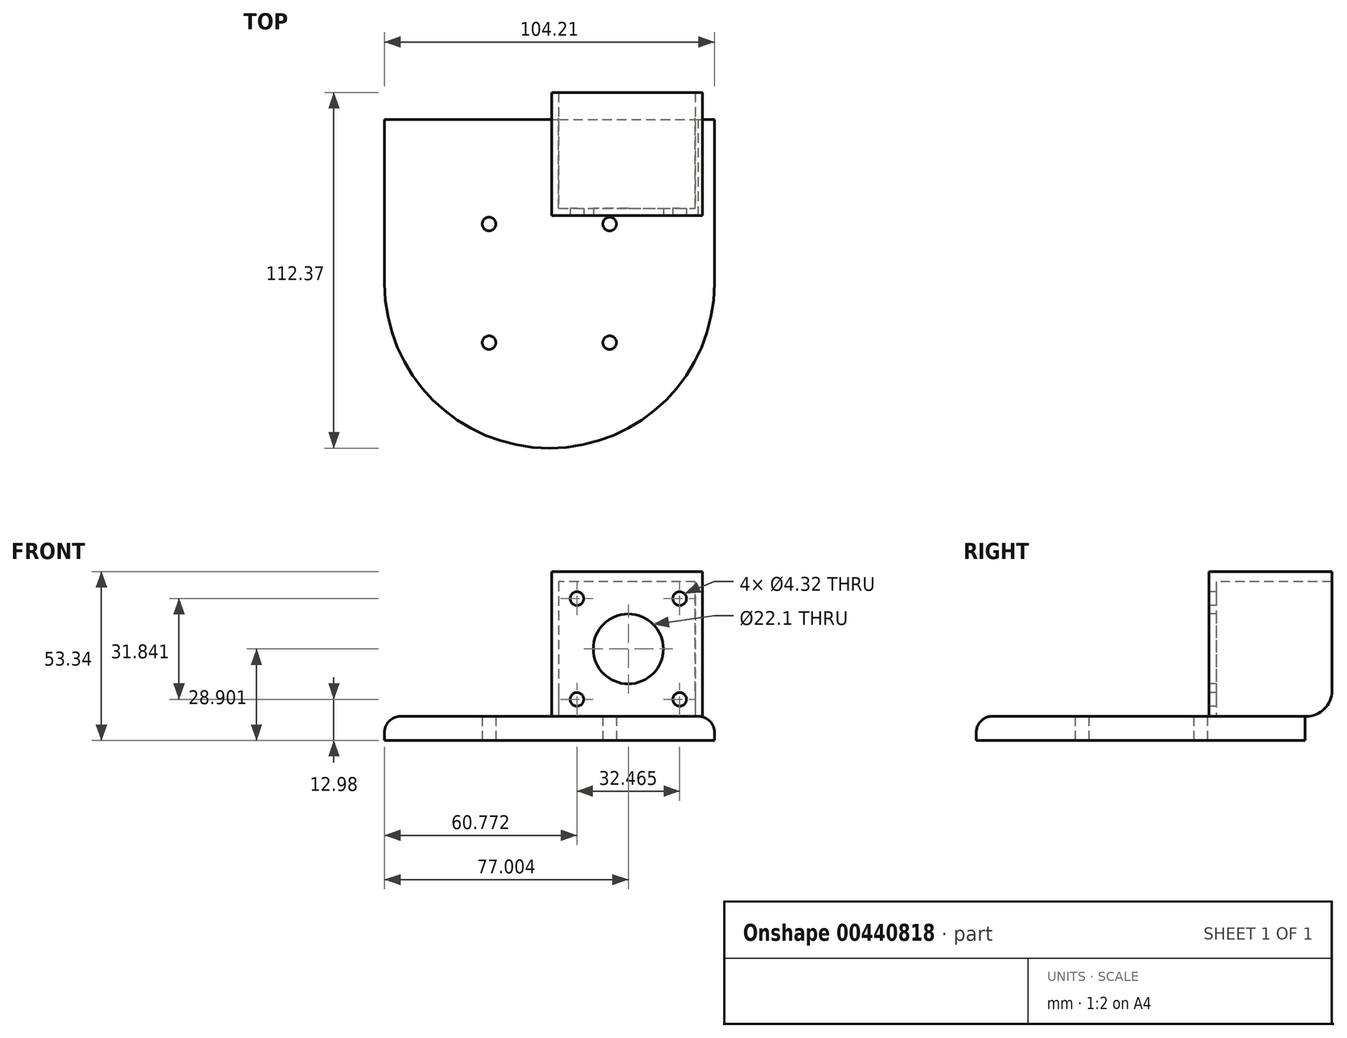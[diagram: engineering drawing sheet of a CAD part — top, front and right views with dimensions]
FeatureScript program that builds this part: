
annotation { "Feature Type Name" : "Feature", "Feature Type Description" : "" }
export const myFeature = defineFeature(function(context is Context, id is Id, definition is map)
    precondition{}
    {
        {
            var Q0;
            Q0=qCreatedBy(makeId("Top.planeOp"),FACE);
            var sketch = newSketch(context, id + "F0", { "sketchPlane" : qUnion([Q0])});
            skLineSegment(sketch, "E0.bottom", {"start": v(19.05, 18.75) * mm, "end": v(-19.05, 18.75) * mm});
            skLineSegment(sketch, "E0.top", {"start": v(19.05, -19.35) * mm, "end": v(-19.05, -19.35) * mm});
            skLineSegment(sketch, "E0.left", {"start": v(19.05, 18.75) * mm, "end": v(19.05, -19.35) * mm});
            skLineSegment(sketch, "E0.right", {"start": v(-19.05, 18.75) * mm, "end": v(-19.05, -19.35) * mm});
            skPoint(sketch, "E0.middle", {"position": v(0, -0.3) * mm});
            skCircle(sketch, "E1", {"center": v(-19.05, 18.75) * mm, "radius": 2.16 * mm});
            skCircle(sketch, "E2.MirrorC", {"center": v(19.05, 18.75) * mm, "radius": 2.16 * mm});
            skCircle(sketch, "E3.MirrorC", {"center": v(19.05, -18.75) * mm, "radius": 2.16 * mm});
            skCircle(sketch, "E4.MirrorC", {"center": v(-19.05, -18.75) * mm, "radius": 2.16 * mm});
            skLineSegment(sketch, "E5.bottom", {"start": v(-52.07, 0) * mm, "end": v(52.14, 0) * mm});
            skLineSegment(sketch, "E5.top", {"start": v(-52.07, 51.72) * mm, "end": v(52.14, 51.72) * mm});
            skLineSegment(sketch, "E5.left", {"start": v(-52.07, 0) * mm, "end": v(-52.07, 51.72) * mm});
            skLineSegment(sketch, "E5.right", {"start": v(52.14, 0) * mm, "end": v(52.14, 51.72) * mm});
            skArc(sketch, "E6", {"start": v(-52.07, 0) * mm, "mid": v(0.03, -52.1) * mm, "end": v(52.14, 0) * mm});
            skSolve(sketch);
        }
        {
            var Q0;
            Q0 = qSketchRegion(id + "F0", true);
            var Q1;
            {var subQ5=sQuery(id+"F0.wireOp",EDGE,"E2.MirrorC");var subQ13=sQuery(id+"F0.wireOp",EDGE,"E0.bottom");var subQ14=makeQuery(id+"F0.imprint","INTERSECT",VERTEX,{"derivedFrom":[subQ13,subQ5]});Q1=makeQuery(id+"F0.imprint","IMPRINT",FACE,{"disambiguationData":[TD([[makeQuery(id+"F0.imprint","IMPRINT",EDGE,{"disambiguationData":[TD([[subQ14,-1.0]])],"derivedFrom":subQ13}),1.0]])]});}
            var Q2;
            {var subQ7=sQuery(id+"F0.wireOp",EDGE,"E3.MirrorC");var subQ9=sQuery(id+"F0.wireOp",EDGE,"E0.top");var subQ10=makeQuery(id+"F0.imprint","INTERSECT",VERTEX,{"derivedFrom":[subQ9,subQ7]});Q2=makeQuery(id+"F0.imprint","IMPRINT",FACE,{"disambiguationData":[TD([[makeQuery(id+"F0.imprint","IMPRINT",EDGE,{"disambiguationData":[TD([[subQ10,-1.0]])],"derivedFrom":subQ9}),-1.0]])]});}
            extrude(context, id + "F1", {"entities" : qUnion([Q0, Q1, Q2]), "depth" : 7.62 * mm});
        }
        {
            var Q0;
            Q0=makeQuery(id+"F1.opExtrude","CAP_EDGE",EDGE,{"disambiguationData":[OSD([sQuery(id+"F0.wireOp",EDGE,"E6")])],"isStart":false});
            fillet(context, id + "F2", {"entities" : qUnion([Q0]), "radius" : 5.08 * mm, "tangentPropagation" : true, "allowEdgeOverflow" : false});
        }
        {
            var Q0;
            Q0=makeQuery(id+"F1.opExtrude","CAP_FACE",FACE,{"disambiguationData":[OSD([sQuery(id+"F0.wireOp",EDGE,"LegbURL5-L06y-lJQr-4DTz-lo4QkHgCWNkF"),sQuery(id+"F0.wireOp",EDGE,"E1"),sQuery(id+"F0.wireOp",EDGE,"E2.MirrorC"),sQuery(id+"F0.wireOp",EDGE,"E3.MirrorC"),sQuery(id+"F0.wireOp",EDGE,"E4.MirrorC")])],"isStart":false});
            var sketch = newSketch(context, id + "F3", { "sketchPlane" : qUnion([Q0])});
            skLineSegment(sketch, "E7.bottom", {"start": v(2.95, 23.69) * mm, "end": v(46.13, 23.69) * mm});
            skLineSegment(sketch, "E7.left", {"start": v(2.95, 23.69) * mm, "end": v(2.95, 57.98) * mm});
            skLineSegment(sketch, "E7.right", {"start": v(46.13, 23.69) * mm, "end": v(46.13, 57.98) * mm});
            skPoint(sketch, "E7.middle", {"position": v(24.54, 40.83) * mm});
            skLineSegment(sketch, "E8.bottom", {"start": v(48.4, 21.4) * mm, "end": v(0.69, 21.4) * mm});
            skLineSegment(sketch, "E8.left", {"start": v(48.4, 21.4) * mm, "end": v(48.4, 60.27) * mm});
            skLineSegment(sketch, "E8.right", {"start": v(0.69, 21.4) * mm, "end": v(0.69, 60.27) * mm});
            skLineSegment(sketch, "E9", {"start": v(2.95, 57.98) * mm, "end": v(2.95, 60.27) * mm});
            skLineSegment(sketch, "E10", {"start": v(2.95, 60.27) * mm, "end": v(0.69, 60.27) * mm});
            skLineSegment(sketch, "E11", {"start": v(46.13, 57.98) * mm, "end": v(46.13, 60.27) * mm});
            skLineSegment(sketch, "E12", {"start": v(46.13, 60.27) * mm, "end": v(48.4, 60.27) * mm});
            skSolve(sketch);
        }
        {
            var Q0;
            Q0 = qSketchRegion(id + "F3", true);
            extrude(context, id + "F4", {"entities" : qUnion([Q0]), "operationType" : NewBodyOperationType.ADD, "depth" : 45.72 * mm});
        }
        {
            var Q0;
            Q0=makeQuery(id+"F4.opExtrude","SWEPT_FACE",FACE,{"disambiguationData":[OSD([sQuery(id+"F3.wireOp",EDGE,"E8.bottom")])]});
            var sketch = newSketch(context, id + "F5", { "sketchPlane" : qUnion([Q0])});
            skPoint(sketch, "E13.centerSnap0", {"position": v(1.08, 30.47) * mm});
            skLineSegment(sketch, "E14", {"start": v(8.7, 44.82) * mm, "end": v(1.08, 44.82) * mm});
            skCircle(sketch, "E15", {"center": v(8.7, 44.82) * mm, "radius": 2.16 * mm});
            skLineSegment(sketch, "E16", {"start": v(24.93, 38.95) * mm, "end": v(24.93, 53.33) * mm});
            skCircle(sketch, "E17", {"center": v(24.93, 28.9) * mm, "radius": 11.05 * mm});
            skLineSegment(sketch, "E18", {"start": v(8.7, 46.98) * mm, "end": v(8.7, 53.33) * mm});
            skLineSegment(sketch, "E19.MirrorCS", {"start": v(41.17, 44.82) * mm, "end": v(48.79, 44.82) * mm});
            skLineSegment(sketch, "E20.MirrorCS", {"start": v(41.17, 46.98) * mm, "end": v(41.17, 53.33) * mm});
            skCircle(sketch, "E21.MirrorC", {"center": v(41.17, 44.82) * mm, "radius": 2.16 * mm});
            skLineSegment(sketch, "E22", {"start": v(24.93, 28.9) * mm, "end": v(29.7, 28.9) * mm});
            skCircle(sketch, "E23.MirrorC", {"center": v(41.17, 12.98) * mm, "radius": 2.16 * mm});
            skCircle(sketch, "E24.MirrorC", {"center": v(8.7, 12.98) * mm, "radius": 2.16 * mm});
            skLineSegment(sketch, "E25.MirrorCS", {"start": v(8.7, 10.82) * mm, "end": v(8.7, 4.47) * mm});
            skLineSegment(sketch, "E26.MirrorCS", {"start": v(8.7, 12.98) * mm, "end": v(1.08, 12.98) * mm});
            skLineSegment(sketch, "E27.MirrorCS", {"start": v(41.17, 10.82) * mm, "end": v(41.17, 4.47) * mm});
            skLineSegment(sketch, "E28.MirrorCS", {"start": v(41.17, 12.98) * mm, "end": v(48.79, 12.98) * mm});
            skSolve(sketch);
        }
        {
            var Q0;
            Q0 = qSketchRegion(id + "F5", true);
            extrude(context, id + "F6", {"entities" : qUnion([Q0]), "operationType" : NewBodyOperationType.REMOVE, "oppositeDirection" : true, "depth" : 25.4 * mm});
        }
        {
            var Q0;
            Q0=makeQuery(id+"F4.opExtrude","SWEPT_FACE",FACE,{"disambiguationData":[OSD([sQuery(id+"F3.wireOp",EDGE,"E7.bottom")])]});
            var sketch = newSketch(context, id + "F7", { "sketchPlane" : qUnion([Q0])});
            skLineSegment(sketch, "E29.bottom", {"start": v(-46.13, 53.34) * mm, "end": v(-2.95, 53.34) * mm});
            skLineSegment(sketch, "E29.top", {"start": v(-46.13, 50.17) * mm, "end": v(-2.95, 50.17) * mm});
            skLineSegment(sketch, "E29.left", {"start": v(-46.13, 53.34) * mm, "end": v(-46.13, 50.17) * mm});
            skLineSegment(sketch, "E29.right", {"start": v(-2.95, 53.34) * mm, "end": v(-2.95, 50.17) * mm});
            skSolve(sketch);
        }
        {
            var Q0;
            Q0=makeQuery(id+"F7.imprint","IMPRINT",FACE,{"disambiguationData":[TD([[makeQuery(id+"F7.imprint","IMPRINT",EDGE,{"derivedFrom":sQuery(id+"F7.wireOp",EDGE,"E29.bottom")}),1.0]])]});
            extrude(context, id + "F8", {"entities" : qUnion([Q0]), "operationType" : NewBodyOperationType.ADD, "depth" : 36.58 * mm});
        }
        {
            var Q0;
            Q0=makeQuery(id+"F4.opExtrude","CAP_EDGE",EDGE,{"disambiguationData":[OSD([sQuery(id+"F3.wireOp",EDGE,"E12")])],"isStart":true});
            var Q1;
            Q1=makeQuery(id+"F4.opExtrude","CAP_EDGE",EDGE,{"disambiguationData":[OSD([sQuery(id+"F3.wireOp",EDGE,"E10")])],"isStart":true});
            fillet(context, id + "F9", {"entities" : qUnion([Q0, Q1]), "radius" : 8.03 * mm, "tangentPropagation" : true, "allowEdgeOverflow" : false});
        }
    });
